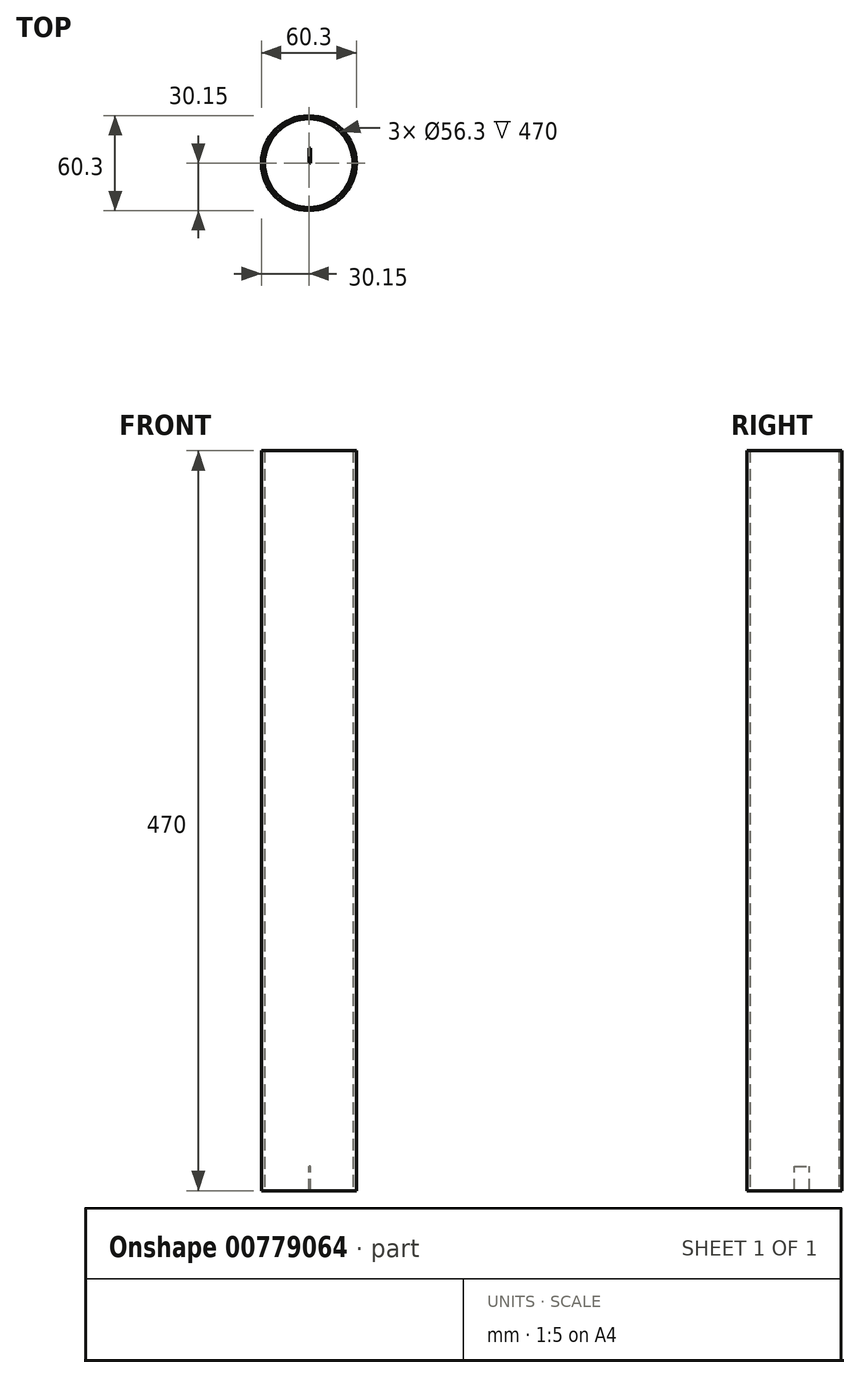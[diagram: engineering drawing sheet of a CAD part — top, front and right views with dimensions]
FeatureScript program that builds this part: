
annotation { "Feature Type Name" : "Feature", "Feature Type Description" : "" }
export const myFeature = defineFeature(function(context is Context, id is Id, definition is map)
    precondition{}
    {
        {
            var Q0;
            Q0=qCreatedBy(makeId("Top.planeOp"),FACE);
            var sketch = newSketch(context, id + "F0", { "sketchPlane" : qUnion([Q0])});
            skCircle(sketch, "E0", {"center": v(0, 0) * mm, "radius": 30.15 * mm});
            skCircle(sketch, "E1", {"center": v(0, 0) * mm, "radius": 28.15 * mm});
            skSolve(sketch);
        }
        {
            var Q0;
            Q0=makeQuery(id+"F0.imprint","IMPRINT",FACE,{"disambiguationData":[TD([[makeQuery(id+"F0.imprint","IMPRINT",EDGE,{"derivedFrom":sQuery(id+"F0.wireOp",EDGE,"E0")}),1.0]])]});
            extrude(context, id + "F1", {"entities" : qUnion([Q0]), "depth" : 470 * mm, "offsetDistance" : 25 * mm});
        }
        {
            var Q0;
            Q0=qCreatedBy(makeId("Right.planeOp"),FACE);
            var sketch = newSketch(context, id + "F2", { "sketchPlane" : qUnion([Q0])});
            skLineSegment(sketch, "E2.bottom", {"start": v(0, 0) * mm, "end": v(9.62, 0) * mm});
            skLineSegment(sketch, "E2.top", {"start": v(0, 15.46) * mm, "end": v(9.62, 15.46) * mm});
            skLineSegment(sketch, "E2.left", {"start": v(0, 0) * mm, "end": v(0, 15.46) * mm});
            skLineSegment(sketch, "E2.right", {"start": v(9.62, 0) * mm, "end": v(9.62, 15.46) * mm});
            skSolve(sketch);
        }
        {
            var Q0;
            Q0 = qSketchRegion(id + "F2", true);
            extrude(context, id + "F3", {"entities" : qUnion([Q0]), "depth" : 1 * mm, "offsetDistance" : 25 * mm});
        }
    });
